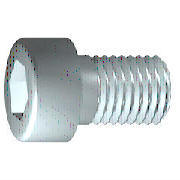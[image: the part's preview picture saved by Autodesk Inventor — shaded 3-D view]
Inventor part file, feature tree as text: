
AUTODESK INVENTOR PART (.ipt)
format: ipt  version: 2015 SP1 (Build 190203100, 203)  size: 190,976 bytes
history: native  units: mm (DEFAULTED — no unit token found)
features: sketch x2, extrude x1, plane x1, fillet x1
ambient origin geometry x7: Origin, YZ Plane, XY Plane, X Axis, Y Axis, Z Axis, Center Point
bodies: Solid1 (feature_tree), Body (feature_tree)
feature tree (5):
  extrude  "Slot"  Depth=8.0mm
  plane  "Work Plane1"
  fillet  "Fillet2"  Radius=8.0mm
  sketch  "Sketch1"  dims[d1=16.875mm d2=0.766912mm d3=8.0mm]
  sketch  "Sketch2"  dims[d4=4.0mm d5=60.0deg d6=8.0mm d7=8.0mm d8=6.928203mm d9=13.0mm d10=90.0deg d11=10.0mm d12=0.0mm d13=16.875mm d14=0.0mm d15=0.766813mm d16=0.766813mm d17=0.8mm d19=0.0mm d26=20.0mm d27=45.0deg d28=0.0mm d29=0.0mm d30=0.1mm]
